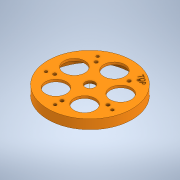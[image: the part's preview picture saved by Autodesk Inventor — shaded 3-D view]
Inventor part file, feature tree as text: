
AUTODESK INVENTOR PART (.ipt)
format: ipt  version: 2022.1 (Build 261234000, 234)  size: 272,896 bytes
history: native  units: in
note: dims shown in document units (in); Inventor stores cm internally (conversion verified against a paired STEP export)
features: sketch x6, extrude x4, hole x2
ambient origin geometry x8: Origin, YZ Plane, XZ Plane, XY Plane, X Axis, Y Axis, Z Axis, Center Point
bodies: Body1 (feature_tree)
feature tree (12):
  extrude  "Extrusion5"  Depth=0.125in
  extrude  "Extrusion6"  Depth=4.0in
  extrude  "Extrusion7"  TaperAngle=0.0deg  [1 undecoded]
  extrude  "Extrusion8"  TaperAngle=0.0deg  [1 undecoded]
  hole  "Hole2"  [1 undecoded]
  hole  "Hole4"  [1 undecoded]
  sketch  "Sketch1"  dims[d5=360.0deg d23=0.125in]
  sketch  "Sketch5"  dims[d24=0.0in d25=4.0in]
  sketch  "Sketch6"  dims[d26=0.04in d27=0.0in]
  sketch  "Sketch8"  dims[d28=0.51in d29=0.0in d30=0.0in]
  sketch  "Sketch9"  dims[d38=4.5015in d39=0.1in]
  sketch  "Sketch11"  dims[d40=0.375in d41=0.0in d42=3.0in d43=1.9685in d45=360.0deg d47=0.177in d48=0.75in d49=0.332in d50=0.25in d51=0.5635in d52=1.0in d53=0.8108in d54=0.1237in d63=0.3825in d64=1.9685in d66=360.0deg d68=0.15in d69=0.75in d70=0.375in d71=0.25in d72=0.5635in d73=1.0in d74=0.8108in]
note: 4 required parameter values undecoded (feature->parameter linkage not recoverable at this tier; creation-order binding heuristic only, values carry confidence <= 0.55)
